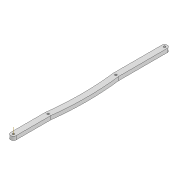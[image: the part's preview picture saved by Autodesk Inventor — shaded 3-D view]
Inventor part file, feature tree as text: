
AUTODESK INVENTOR PART (.ipt)
format: ipt  version: 2022 (Build 260153000, 153)  size: 102,400 bytes
history: native  units: mm
features: extrude x1, other x1, sketch x1
ambient origin geometry x8: Origin, YZ Plane, XZ Plane, XY Plane, X Axis, Y Axis, Z Axis, Center Point
bodies: Solid1 (feature_tree)
feature tree (3):
  extrude  "Extrusion1"  Depth=300.0mm
  other  "Work Axis2"
  sketch  "Sketch1"  dims[d0=2.2mm d1=2.2mm d2=6.0mm d3=163.527mm d4=2.2mm d5=37.565mm d6=4.0mm d7=0.0mm d8=2.2mm d9=110.762mm d10=300.0mm d11=300.0mm]
